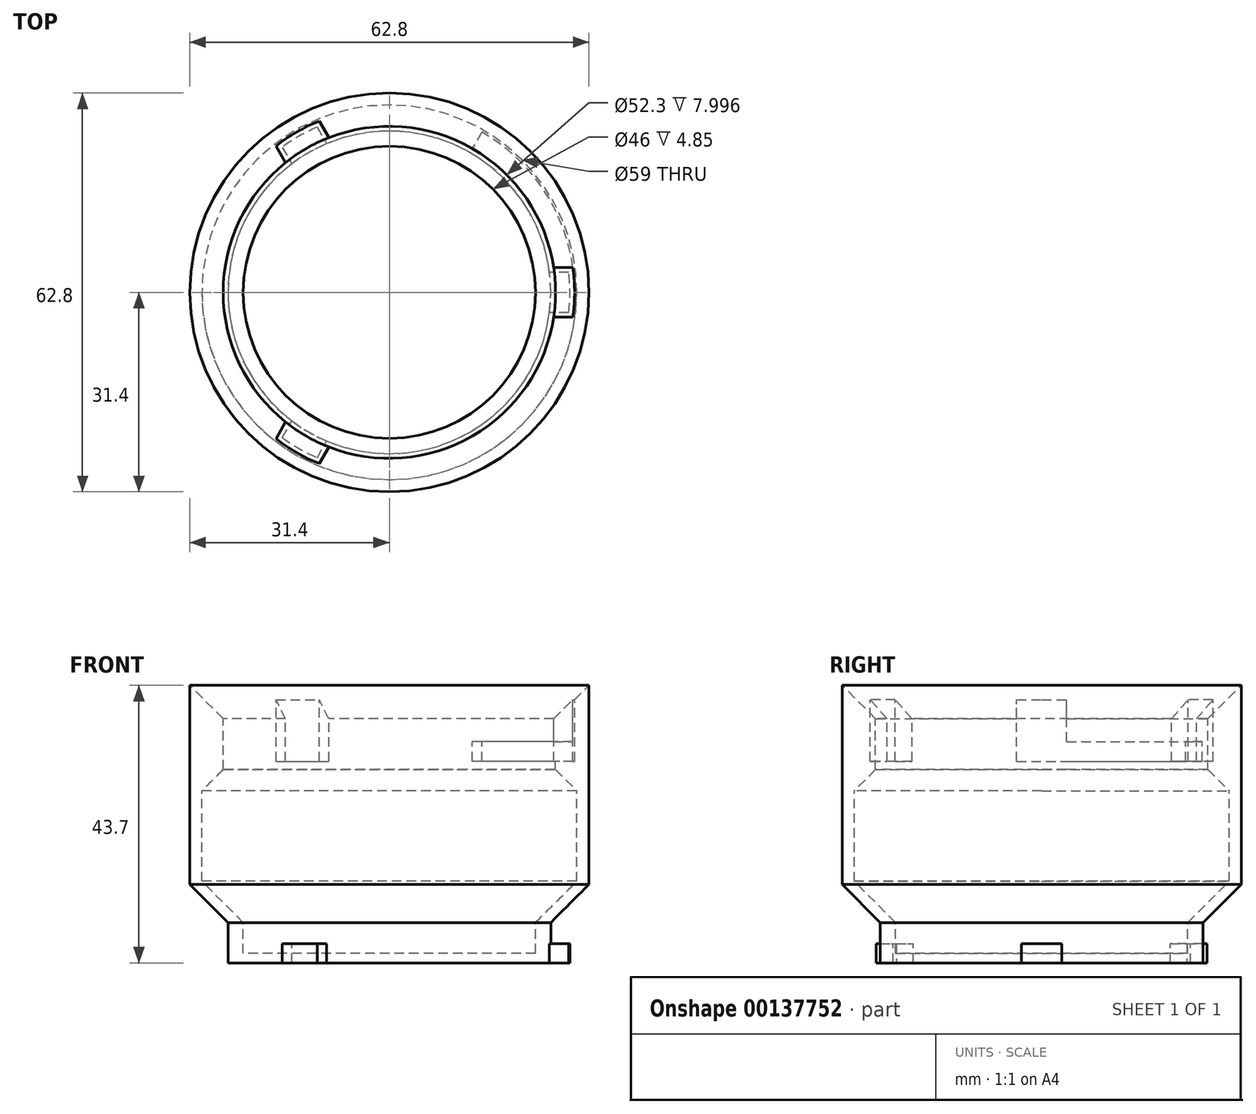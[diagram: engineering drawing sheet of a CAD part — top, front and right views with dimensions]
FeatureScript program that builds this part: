
annotation { "Feature Type Name" : "Feature", "Feature Type Description" : "" }
export const myFeature = defineFeature(function(context is Context, id is Id, definition is map)
    precondition{}
    {
        {
            var Q0;
            Q0=qCreatedBy(makeId("Top.planeOp"),FACE);
            var sketch = newSketch(context, id + "F0", { "sketchPlane" : qUnion([Q0])});
            skCircle(sketch, "E0", {"center": v(0, 0) * mm, "radius": 25.4 * mm});
            skSolve(sketch);
        }
        {
            var Q0;
            Q0 = qSketchRegion(id + "F0", true);
            extrude(context, id + "F1", {"entities" : qUnion([Q0]), "oppositeDirection" : true, "depth" : 6.35 * mm});
        }
        {
            var Q0;
            Q0=makeQuery(id+"F1.opExtrude","CAP_FACE",FACE,{"disambiguationData":[OSD([sQuery(id+"F0.wireOp",EDGE,"E0")])],"isStart":false});
            var sketch = newSketch(context, id + "F2", { "sketchPlane" : qUnion([Q0])});
            skLineSegment(sketch, "E1", {"start": v(0, 0) * mm, "end": v(48.01, 0) * mm, "construction": true});
            skLineSegment(sketch, "E2.bottom", {"start": v(28.22, 3.18) * mm, "end": v(22.4, 3.18) * mm});
            skLineSegment(sketch, "E2.top", {"start": v(28.22, -3.18) * mm, "end": v(22.4, -3.18) * mm});
            skLineSegment(sketch, "E2.right", {"start": v(22.4, 3.17) * mm, "end": v(22.4, -3.18) * mm});
            skPoint(sketch, "E2.middle", {"position": v(25.4, 0) * mm});
            skArc(sketch, "E3", {"start": v(28.22, -3.18) * mm, "mid": v(28.4, 0) * mm, "end": v(28.22, 3.17) * mm});
            skLineSegment(sketch, "E4.1.0", {"start": v(-11.36, 26.03) * mm, "end": v(-8.45, 20.99) * mm});
            skArc(sketch, "E4.1.1", {"start": v(-11.36, 26.03) * mm, "mid": v(-14.2, 24.6) * mm, "end": v(-16.86, 22.85) * mm});
            skLineSegment(sketch, "E4.1.2", {"start": v(-13.95, 17.81) * mm, "end": v(-8.45, 20.99) * mm});
            skLineSegment(sketch, "E4.1.3", {"start": v(-16.86, 22.85) * mm, "end": v(-13.95, 17.81) * mm});
            skPoint(sketch, "E4.1.4", {"position": v(-12.7, 22) * mm});
            skLineSegment(sketch, "E4.1.5", {"start": v(0, 0) * mm, "end": v(-24, 41.58) * mm, "construction": true});
            skLineSegment(sketch, "E4.2.0", {"start": v(-16.86, -22.85) * mm, "end": v(-13.95, -17.81) * mm});
            skArc(sketch, "E4.2.1", {"start": v(-16.86, -22.85) * mm, "mid": v(-14.2, -24.6) * mm, "end": v(-11.36, -26.03) * mm});
            skLineSegment(sketch, "E4.2.2", {"start": v(-8.45, -20.99) * mm, "end": v(-13.95, -17.81) * mm});
            skLineSegment(sketch, "E4.2.3", {"start": v(-11.36, -26.03) * mm, "end": v(-8.45, -20.99) * mm});
            skPoint(sketch, "E4.2.4", {"position": v(-12.7, -22) * mm});
            skLineSegment(sketch, "E4.2.5", {"start": v(0, 0) * mm, "end": v(-24, -41.58) * mm, "construction": true});
            skSolve(sketch);
        }
        {
            var Q0;
            Q0 = qSketchRegion(id + "F2", true);
            extrude(context, id + "F3", {"entities" : qUnion([Q0]), "operationType" : NewBodyOperationType.ADD, "oppositeDirection" : true, "depth" : 3 * mm});
        }
        {
            var Q0;
            Q0=makeQuery(id+"F1.opExtrude","CAP_FACE",FACE,{"disambiguationData":[OSD([sQuery(id+"F0.wireOp",EDGE,"E0")])],"isStart":true});
            var sketch = newSketch(context, id + "F4", { "sketchPlane" : qUnion([Q0])});
            skCircle(sketch, "E5", {"center": v(0, 0) * mm, "radius": 22.4 * mm});
            skSolve(sketch);
        }
        {
            var Q0;
            Q0 = qSketchRegion(id + "F4", true);
            var Q1;
            Q1=makeQuery(id+"F3.opExtrude","CAP_FACE",FACE,{"disambiguationData":[OSD([sQuery(id+"F2.wireOp",EDGE,"E4.1.0"),sQuery(id+"F2.wireOp",EDGE,"E4.1.1"),sQuery(id+"F2.wireOp",EDGE,"E4.1.2"),sQuery(id+"F2.wireOp",EDGE,"E4.1.3")])],"isStart":false});
            extrude(context, id + "F5", {"entities" : qUnion([Q0]), "operationType" : NewBodyOperationType.REMOVE, "endBound" : BoundingType.UP_TO_SURFACE, "oppositeDirection" : true, "endBoundEntityFace" : qUnion([Q1]), "depth" : 3 * mm});
        }
        {
            var Q0;
            Q0=makeQuery(id+"F1.opExtrude","CAP_FACE",FACE,{"disambiguationData":[OSD([sQuery(id+"F0.wireOp",EDGE,"E0")])],"isStart":true});
            var sketch = newSketch(context, id + "F6", { "sketchPlane" : qUnion([Q0])});
            skCircle(sketch, "E6", {"center": v(0, 0) * mm, "radius": 31.4 * mm});
            skCircle(sketch, "E7", {"center": v(0, 0) * mm, "radius": 22.4 * mm});
            skSolve(sketch);
        }
        {
            var Q0;
            Q0 = qSketchRegion(id + "F6", true);
            extrude(context, id + "F7", {"entities" : qUnion([Q0]), "operationType" : NewBodyOperationType.ADD, "depth" : 31.75 * mm});
        }
        {
            var Q0;
            Q0=makeQuery(id+"F7.opExtrude","CAP_FACE",FACE,{"disambiguationData":[OSD([sQuery(id+"F6.wireOp",EDGE,"E6"),sQuery(id+"F6.wireOp",EDGE,"E7")])],"isStart":false});
            var sketch = newSketch(context, id + "F8", { "sketchPlane" : qUnion([Q0])});
            skLineSegment(sketch, "E8", {"start": v(0, 0) * mm, "end": v(51.24, 0) * mm, "construction": true});
            skArc(sketch, "E9", {"start": v(28.88, -3.92) * mm, "mid": v(29.15, 0) * mm, "end": v(28.88, 3.93) * mm});
            skLineSegment(sketch, "E10", {"start": v(28.88, 3.93) * mm, "end": v(17.45, 3.93) * mm});
            skLineSegment(sketch, "E11", {"start": v(17.45, 3.93) * mm, "end": v(17.45, 0) * mm});
            skLineSegment(sketch, "E12.MirrorCS", {"start": v(17.45, -3.93) * mm, "end": v(17.45, 0) * mm});
            skLineSegment(sketch, "E13.MirrorCS", {"start": v(28.88, -3.93) * mm, "end": v(17.45, -3.93) * mm});
            skLineSegment(sketch, "E14.1.0", {"start": v(-11.04, 26.98) * mm, "end": v(-5.33, 17.07) * mm});
            skLineSegment(sketch, "E14.1.1", {"start": v(-12.12, 13.15) * mm, "end": v(-8.72, 15.11) * mm});
            skLineSegment(sketch, "E14.1.2", {"start": v(-5.33, 17.07) * mm, "end": v(-8.72, 15.11) * mm});
            skLineSegment(sketch, "E14.1.3", {"start": v(-17.84, 23.05) * mm, "end": v(-12.12, 13.15) * mm});
            skLineSegment(sketch, "E14.1.4", {"start": v(0, 0) * mm, "end": v(-25.62, 44.37) * mm, "construction": true});
            skArc(sketch, "E14.1.5", {"start": v(-11.04, 26.98) * mm, "mid": v(-14.57, 25.24) * mm, "end": v(-17.84, 23.05) * mm});
            skLineSegment(sketch, "E14.2.0", {"start": v(-17.84, -23.05) * mm, "end": v(-12.12, -13.15) * mm});
            skLineSegment(sketch, "E14.2.1", {"start": v(-5.33, -17.07) * mm, "end": v(-8.72, -15.11) * mm});
            skLineSegment(sketch, "E14.2.2", {"start": v(-12.12, -13.15) * mm, "end": v(-8.72, -15.11) * mm});
            skLineSegment(sketch, "E14.2.3", {"start": v(-11.04, -26.98) * mm, "end": v(-5.33, -17.07) * mm});
            skLineSegment(sketch, "E14.2.4", {"start": v(0, 0) * mm, "end": v(-25.62, -44.37) * mm, "construction": true});
            skArc(sketch, "E14.2.5", {"start": v(-17.84, -23.05) * mm, "mid": v(-14.58, -25.24) * mm, "end": v(-11.04, -26.98) * mm});
            skSolve(sketch);
        }
        {
            var Q0;
            Q0 = qSketchRegion(id + "F8", true);
            extrude(context, id + "F9", {"entities" : qUnion([Q0]), "operationType" : NewBodyOperationType.REMOVE, "oppositeDirection" : true, "depth" : 6.35 * mm});
        }
        {
            var Q0;
            Q0=makeQuery(id+"F7.opExtrude","CAP_FACE",FACE,{"disambiguationData":[OSD([sQuery(id+"F6.wireOp",EDGE,"E6"),sQuery(id+"F6.wireOp",EDGE,"E7")])],"isStart":false});
            var sketch = newSketch(context, id + "F10", { "sketchPlane" : qUnion([Q0])});
            skCircle(sketch, "E15", {"center": v(0, 0) * mm, "radius": 26.15 * mm});
            skSolve(sketch);
        }
        {
            var Q0;
            Q0 = qSketchRegion(id + "F10", true);
            extrude(context, id + "F11", {"entities" : qUnion([Q0]), "operationType" : NewBodyOperationType.REMOVE, "oppositeDirection" : true, "depth" : 28 * mm});
        }
        {
            var Q0;
            Q0=qCreatedBy(makeId("Front.planeOp"),FACE);
            var sketch = newSketch(context, id + "F12", { "sketchPlane" : qUnion([Q0])});
            skLineSegment(sketch, "E16.bottom", {"start": v(29.15, 25.4) * mm, "end": v(18.75, 25.4) * mm});
            skLineSegment(sketch, "E16.top", {"start": v(29.15, 28.5) * mm, "end": v(18.75, 28.5) * mm});
            skLineSegment(sketch, "E16.left", {"start": v(29.15, 25.4) * mm, "end": v(29.15, 28.5) * mm});
            skLineSegment(sketch, "E16.right", {"start": v(18.75, 25.4) * mm, "end": v(18.75, 28.5) * mm});
            skSolve(sketch);
        }
        {
            var Q0;
            Q0=makeQuery(id+"F7.opExtrude","CAP_FACE",FACE,{"disambiguationData":[OSD([sQuery(id+"F6.wireOp",EDGE,"E6"),sQuery(id+"F6.wireOp",EDGE,"E7")])],"isStart":false});
            var sketch = newSketch(context, id + "F13", { "sketchPlane" : qUnion([Q0])});
            skArc(sketch, "E17", {"start": v(37.43, 0) * mm, "mid": v(32.41, 18.71) * mm, "end": v(18.71, 32.41) * mm});
            skLineSegment(sketch, "E18", {"start": v(0, 0) * mm, "end": v(24.7, 42.78) * mm, "construction": true});
            skLineSegment(sketch, "E19", {"start": v(0, 0) * mm, "end": v(60.15, 0) * mm, "construction": true});
            skSolve(sketch);
        }
        {
            var Q0;
            Q0 = qSketchRegion(id + "F12", true);
            var Q1;
            Q1 = qConstructionFilter(qBodyType(qCreatedBy(id + "F13" ,EDGE), BodyType.WIRE), ConstructionObject.NO);
            sweep(context, id + "F14", {"operationType" : NewBodyOperationType.REMOVE, "profiles" : qUnion([Q0]), "path" : qUnion([Q1])});
        }
        {
            var Q0;
            Q0=qCreatedBy(makeId("Front.planeOp"),FACE);
            var sketch = newSketch(context, id + "F15", { "sketchPlane" : qUnion([Q0])});
            skLineSegment(sketch, "E20", {"start": v(0, 0) * mm, "end": v(0, 75.04) * mm});
            skSolve(sketch);
        }
        {
            var Q0;
            Q0=makeQuery(id+"F7.opExtrude","CAP_EDGE",EDGE,{"disambiguationData":[OSD([sQuery(id+"F6.wireOp",EDGE,"E6")])],"isStart":true});
            chamfer(context, id + "F16", {"entities" : qUnion([Q0]), "width" : 6 * mm, "tangentPropagation" : true});
        }
        {
            var Q0;
            Q0=makeQuery(id+"F7.opExtrude","CAP_FACE",FACE,{"disambiguationData":[OSD([sQuery(id+"F6.wireOp",EDGE,"E6"),sQuery(id+"F6.wireOp",EDGE,"E7")])],"isStart":false});
            var sketch = newSketch(context, id + "F17", { "sketchPlane" : qUnion([Q0])});
            skCircle(sketch, "E21", {"center": v(0, 0) * mm, "radius": 31.4 * mm});
            skCircle(sketch, "E22", {"center": v(0, 0) * mm, "radius": 26.15 * mm});
            skSolve(sketch);
        }
        {
            var Q0;
            Q0 = qSketchRegion(id + "F17", true);
            extrude(context, id + "F18", {"entities" : qUnion([Q0]), "operationType" : NewBodyOperationType.ADD, "depth" : 6.35 * mm});
        }
        {
            var Q0;
            Q0=makeQuery(id+"F18.opExtrude","CAP_EDGE",EDGE,{"disambiguationData":[OSD([sQuery(id+"F17.wireOp",EDGE,"E22")])],"isStart":false});
            chamfer(context, id + "F19", {"entities" : qUnion([Q0]), "width" : 6 * mm, "tangentPropagation" : true});
        }
        {
            var Q0;
            Q0 = qSketchRegion(id + "F8", true);
            extrude(context, id + "F20", {"entities" : qUnion([Q0]), "operationType" : NewBodyOperationType.REMOVE, "depth" : 25 * mm});
        }
        {
            var Q0;
            Q0=qCreatedBy(makeId("Front.planeOp"),FACE);
            var sketch = newSketch(context, id + "F21", { "sketchPlane" : qUnion([Q0])});
            skLineSegment(sketch, "E23", {"start": v(0, -4.85) * mm, "end": v(23, -4.85) * mm});
            skLineSegment(sketch, "E24", {"start": v(23, -4.85) * mm, "end": v(23, 0) * mm});
            skLineSegment(sketch, "E25", {"start": v(23, 0) * mm, "end": v(29.5, 6.5) * mm});
            skLineSegment(sketch, "E26", {"start": v(29.5, 6.5) * mm, "end": v(29.5, 20.75) * mm});
            skLineSegment(sketch, "E27", {"start": v(29.5, 20.75) * mm, "end": v(25.85, 24.4) * mm});
            skLineSegment(sketch, "E28", {"start": v(25.85, 24.4) * mm, "end": v(0, 24.4) * mm});
            skLineSegment(sketch, "E29", {"start": v(0, 24.4) * mm, "end": v(0, 0) * mm});
            skLineSegment(sketch, "E30", {"start": v(0, 0) * mm, "end": v(0, -4.85) * mm});
            skSolve(sketch);
        }
        {
            var Q0;
            Q0 = qSketchRegion(id + "F21", true);
            var Q1;
            Q1 = qConstructionFilter(qBodyType(qCreatedBy(id + "F21" ,EDGE), BodyType.WIRE), ConstructionObject.NO);
            var Q2;
            Q2=sQuery(id+"F15.wireOp",EDGE,"E20");
            revolve(context, id + "F22", {"operationType" : NewBodyOperationType.REMOVE, "entities" : qUnion([Q0]), "surfaceEntities" : qUnion([Q1]), "axis" : qUnion([Q2]), "revolveType" : RevolveType.FULL, "oppositeDirection" : true});
        }
    });
